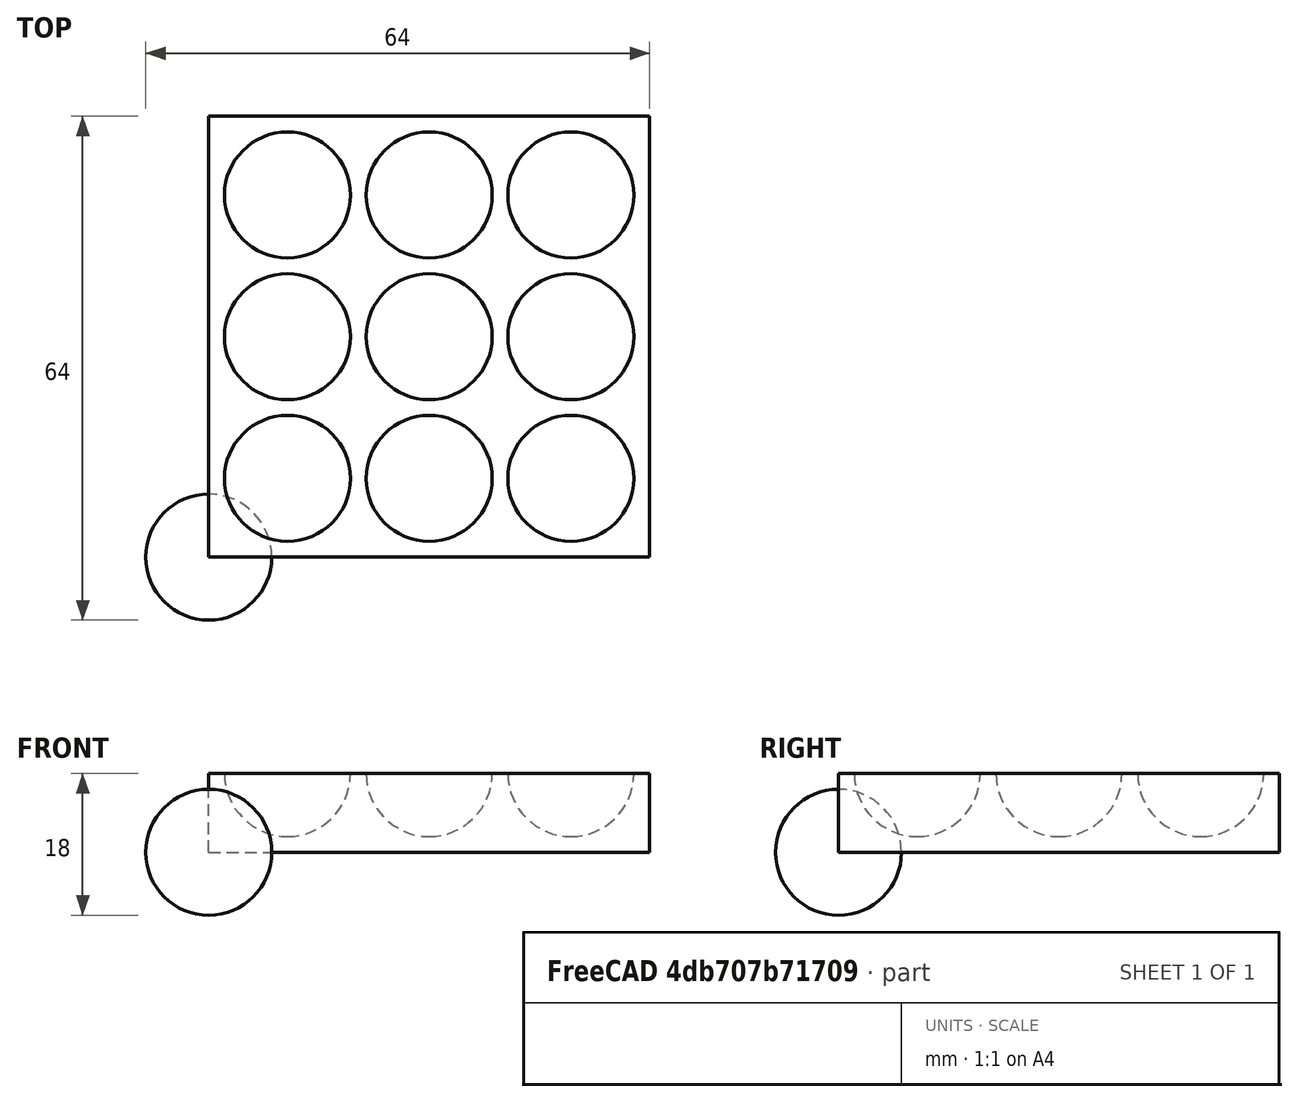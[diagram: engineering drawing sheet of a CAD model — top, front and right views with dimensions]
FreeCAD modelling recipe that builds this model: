
FCSTD DOCUMENT  (FreeCAD 0.21R33771 (Git))
Label: OJT1_T13P01_porta-bales
License: All rights reserved
LicenseURL: http://en.wikipedia.org/wiki/All_rights_reserved
objects: Part::Cut×2, Part::Sphere×1, Part::FeaturePython×1, Part::Box×1
note: 4 computed .brp shape members not serialized (recipe doc carries the construction recipe); baked Part::Feature solids carry a one-line shape summary decoded from their .brp

FEATURE [Part::Sphere] Sphere
  Angle1 = -90
  Angle2 = 90
  Angle3 = 360
  AttacherType = Attacher::AttachEngine3D
  Radius = 8
FEATURE [Part::FeaturePython] Array  # Draft array (typed FeaturePython)
  AlwaysSyncPlacement = false
  Angle = 360
  ArrayType = 0
  Axis = (0,0,1)
  Base = -> Sphere
  Center = (0,0,0)
  Count = 9
  ExpandArray = false
  Fuse = false
  IntervalAxis = (0,0,0)
  IntervalX = (18,0,0)
  IntervalY = (0,18,0)
  IntervalZ = (0,0,100)
  NumberCircles = 3
  NumberPolar = 5
  NumberX = 3
  NumberY = 3
  NumberZ = 1
  Placement = pos=(10,10,10) rot=(0,0,1;0rad)
  PlacementList = 9 placements: [(0,0,0),(0,18,0),(0,36,0),(18,0,0),(18,18,0),(18,36,0),(36,0,0),(36,18,0),(36,36,0)]
  RadialDistance = 50
  ScaleList = (9) [(1,1,1),(1,1,1),(1,1,1),(1,1,1),(1,1,1),(1,1,1),(1,1,1),(1,1,1),(1,1,1)]
  Symmetry = 1
  TangentialDistance = 25
FEATURE [Part::Box] Box  label="Cube"
  AttacherType = Attacher::AttachEngine3D
  Height = 10
  Length = 56
  Placement = pos=(-10,-10,-10) rot=(0,0,1;0rad)
  Width = 56
FEATURE [Part::Cut] Cut
  Base = -> Box
  Placement = pos=(10,10,10) rot=(0,0,1;0rad)
  Refine = true
  Tool = -> Array
FEATURE [Part::Cut] Cut001  label="porta-bales"
  Base = -> Cut
  Refine = true
  Tool = -> Array
